# Revit family: L44
name_source: partatom
category: Lighting Fixtures
revit_build: Autodesk Revit Architecture 2012 (Build: 20110309_2315(x64)
units: mm (PartAtom-declared; Revit-internal decimal feet)

## types (3) — shared parameters
Apparent Load = 20 VA
Circuiting = 1 Circuit
Color Filter = 16777215
Default Elevation = 4' - 0"
Description = Mod™ 44 LED Recessed
Dimming = D10
Dimming Lamp Color Temperature Shift = <None>
Distribution = Direct
Emit Shape Visible in Rendering = No
Emit from Rectangle Length = 3' - 10"
Emit from Rectangle Width = 0' - 3 1/2"
Is 120V = No
Is 277V = Yes
Lamp = LED Lamp
Length = 4' - 0"
Load Classification = Lighting
Manufacturer = Litecontrol Lighting
Manufacturer Fax = 781-293-2849
Material Finish = Hubbell - Paint - White
Model = L44
Opal lens = Hubbell - Glass
Product Documentation Link = http://www.litecontrol.com
Product Page URL = http://www.litecontrol.com
Tilt Angle = -90.00°
URL = http://www.litecontrol.com
Voltage = 277 V
Wattage Comments = 20W-23.2W
Watts = 20 W
zzLength1 = 0' - 5 5/8"

## per-type parameters (varying)
| type | Photometric Web File |
| 44L-xx-D-04-SGL-Cx-35K-D040 (AGI) | 44L-xx-D-04-SGL-Cx-35K-D040 (AGI).ies |
| 44L-xx-D-04-SGL-Cx-35K-D050 (AGI) | 44L-xx-D-04-SGL-Cx-35K-D050 (AGI).ies |
| 44L-xx-D-04-SGL-Cx-35K-D075 (AGI) | 44L-xx-D-04-SGL-Cx-35K-D075 (AGI).ies |

## geometry (parser evidence)
native form markers: Sweep x5
no freeform markers — native parametric forms only
